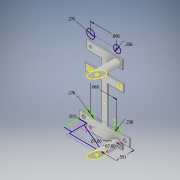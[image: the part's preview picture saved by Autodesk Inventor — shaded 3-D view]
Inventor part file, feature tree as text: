
AUTODESK INVENTOR PART (.ipt)
format: ipt  version: 2018 (Build 220112000, 112)  size: 278,528 bytes
history: native  units: in
note: dims shown in document units (in); Inventor stores cm internally (conversion verified against a paired STEP export)
features: extrude x10, sketch x8
ambient origin geometry x8: Origin, YZ Plane, XZ Plane, XY Plane, X Axis, Y Axis, Z Axis, Center Point
bodies: Solid1 (feature_tree)
feature tree (18):
  extrude  "Extrusion1"  Depth=1.2598in
  extrude  "Extrusion2"  TaperAngle=0.0deg  [1 undecoded]
  extrude  "Extrusion3"  Depth=0.2362in
  extrude  "Extrusion5"  Depth=0.0394in TaperAngle=0.0deg
  extrude  "Extrusion6"  Depth=0.6791in
  extrude  "Extrusion9"  Depth=0.1181in
  extrude  "Extrusion14"  Depth=0.9646in
  extrude  "Extrusion19"  Depth=0.0394in
  extrude  "Extrusion20"  Depth=0.0394in
  extrude  "Extrusion21"  Depth=0.0394in
  sketch  "Sketch18"  dims[d18=0.4823in d19=0.4823in d20=0.1181in d21=0.1181in d22=0.0787in d23=0.0in d28=2.2835in d30=0.0in d31=0.0in d32=0.1969in d33=1.1811in d34=1.1811in d35=0.2756in d36=0.2756in d37=0.0787in d38=0.0787in d39=0.0787in d40=0.0787in d41=0.9055in d42=0.9055in d43=0.4528in d44=0.4528in d45=0.4528in d46=0.4528in d47=0.0394in d48=0.0in d52=0.2756in d55=0.2756in d57=0.0787in d58=0.0in d59=0.2362in d60=0.2362in d61=0.2362in d62=0.2362in d63=0.0787in d64=0.0in d65=1.4567in d66=1.4567in d72=0.4604in d73=0.25in d74=0.0in d97=0.2362in d98=0.8661in d99=0.2362in d100=0.8661in d101=0.4724in d102=0.0in d116=1.378in d117=0.2362in d118=0.2362in d119=0.2362in d120=0.2362in d121=0.8661in d122=0.8661in d123=0.4331in d124=0.4331in d125=0.4331in d126=0.4331in d139=0.0154in d140=0.5906in d141=0.4604in d152=0.9in d153=0.0in d155=0.5in d156=5.0in d157=0.0in d158=0.1969in d159=0.0in d160=0.0787in d162=0.0787in d163=0.4188in]
  sketch  "Sketch1"  dims[d0=0.1969in d2=1.2598in]
  sketch  "Sketch2"  dims[d3=0.2362in d4=0.0in]
  sketch  "Sketch4"  dims[d5=1.6535in d6=0.2362in]
  sketch  "Sketch6"  dims[d7=0.0in d8=0.0394in d9=0.0in]
  sketch  "Sketch13"  dims[d10=1.3583in d13=0.6791in]
  sketch  "Sketch16"  dims[d14=0.6791in d15=0.1181in]
  sketch  "Sketch17"  dims[d16=0.1181in d17=0.9646in]
note: 1 required parameter value undecoded (feature->parameter linkage not recoverable at this tier; creation-order binding heuristic only, values carry confidence <= 0.55)
